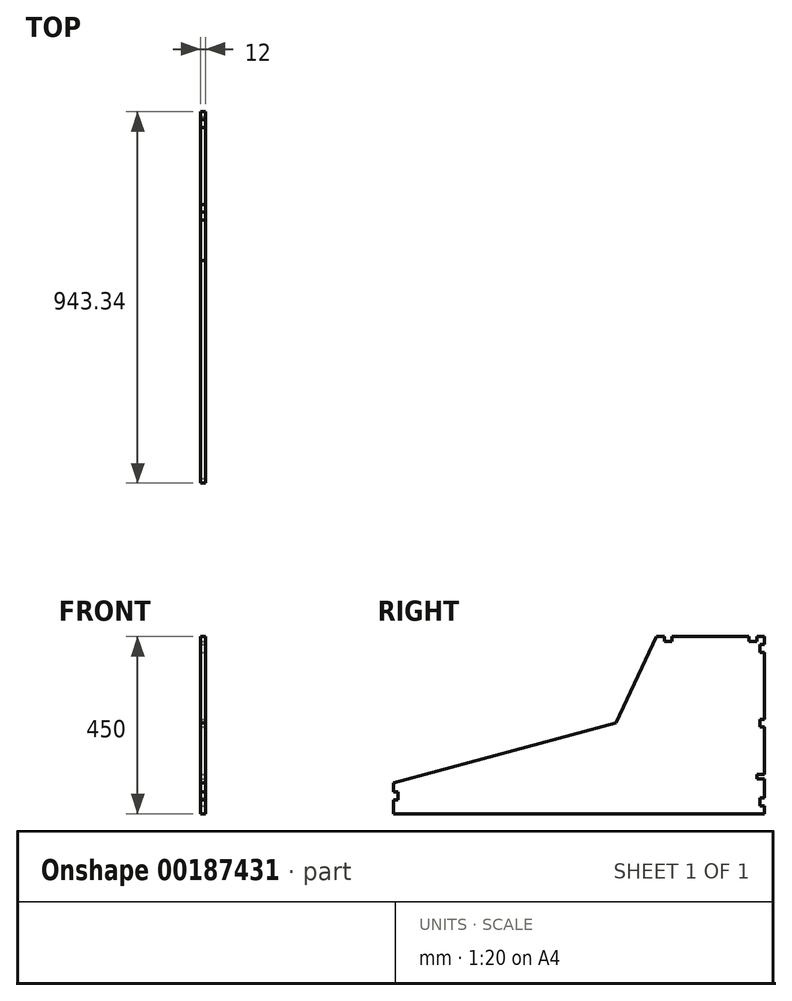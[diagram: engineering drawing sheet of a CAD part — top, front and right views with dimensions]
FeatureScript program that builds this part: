
annotation { "Feature Type Name" : "Feature", "Feature Type Description" : "" }
export const myFeature = defineFeature(function(context is Context, id is Id, definition is map)
    precondition{}
    {
        {
            var Q0;
            Q0=qCreatedBy(makeId("Right.planeOp"),FACE);
            var sketch = newSketch(context, id + "F0", { "sketchPlane" : qUnion([Q0])});
            skLineSegment(sketch, "E0.bottom", {"start": v(0, 0) * mm, "end": v(-738, 0) * mm});
            skLineSegment(sketch, "E0.top", {"start": v(0, 460) * mm, "end": v(-70.38, 460) * mm});
            skLineSegment(sketch, "E0.left", {"start": v(0, 0) * mm, "end": v(0, 460) * mm});
            skLineSegment(sketch, "E0.right", {"start": v(-738, 0) * mm, "end": v(-738, 90) * mm});
            skLineSegment(sketch, "E1", {"start": v(-172.22, 241.6) * mm, "end": v(-738, 90) * mm});
            skLineSegment(sketch, "E2.bottom", {"start": v(0, 0) * mm, "end": v(200, 0) * mm});
            skLineSegment(sketch, "E2.top", {"start": v(0, 460) * mm, "end": v(200, 460) * mm});
            skLineSegment(sketch, "E2.right", {"start": v(200, 0) * mm, "end": v(200, 460) * mm});
            skLineSegment(sketch, "E3", {"start": v(-70.38, 460) * mm, "end": v(-172.22, 241.6) * mm});
            skPoint(sketch, "E4.start.orphan", {"position": v(-850, 0) * mm});
            skSolve(sketch);
        }
        {
            var Q0;
            {var subQ4=sQuery(id+"F0.wireOp",EDGE,"E0.left");Q0=makeQuery(id+"F0.imprint","IMPRINT",FACE,{"disambiguationData":[TD([[makeQuery(id+"F0.imprint","IMPRINT",EDGE,{"derivedFrom":subQ4}),1.0]])]});}
            var Q1;
            {var subQ5=sQuery(id+"F0.wireOp",EDGE,"E1");Q1=makeQuery(id+"F0.imprint","IMPRINT",FACE,{"disambiguationData":[TD([[makeQuery(id+"F0.imprint","IMPRINT",EDGE,{"derivedFrom":subQ5}),1.0]])]});}
            var Q2;
            {var subQ0=sQuery(id+"F0.wireOp",EDGE,"gMac2zyo-H2hs-1GUk-txYp-QcEbhLNx8KIs");Q2=makeQuery(id+"F0.imprint","IMPRINT",FACE,{"disambiguationData":[TD([[makeQuery(id+"F0.imprint","IMPRINT",EDGE,{"derivedFrom":subQ0}),1.0]])]});}
            var Q3;
            Q3=makeQuery(id+"F0.imprint","IMPRINT",FACE,{"disambiguationData":[TD([[makeQuery(id+"F0.imprint","IMPRINT",EDGE,{"derivedFrom":sQuery(id+"F0.wireOp",EDGE,"E2.bottom")}),1.0]])]});
            var Q4;
            {var subQ2=sQuery(id+"F0.wireOp",EDGE,"E0.bottom");Q4=makeQuery(id+"F0.imprint","IMPRINT",FACE,{"disambiguationData":[TD([[makeQuery(id+"F0.imprint","IMPRINT",EDGE,{"derivedFrom":subQ2}),-1.0]])]});}
            var Q5;
            {var subQ0=sQuery(id+"F0.wireOp",EDGE,"gPEywheX-FLUY-aZ3r-SrXT-0dIdcKwJWZQq");Q5=makeQuery(id+"F0.imprint","IMPRINT",FACE,{"disambiguationData":[TD([[makeQuery(id+"F0.imprint","IMPRINT",EDGE,{"derivedFrom":subQ0}),1.0]])]});}
            extrude(context, id + "F1", {"entities" : qUnion([Q0, Q1, Q2, Q3, Q4, Q5]), "depth" : 12 * mm, "offsetDistance" : 25 * mm});
        }
        {
            var Q0;
            Q0=makeQuery(id+"F1.opExtrude","CAP_FACE",FACE,{"disambiguationData":[OSD([sQuery(id+"F0.wireOp",EDGE,"E0.bottom"),sQuery(id+"F0.wireOp",EDGE,"E0.top"),sQuery(id+"F0.wireOp",EDGE,"E0.right"),sQuery(id+"F0.wireOp",EDGE,"gMac2zyo-H2hs-1GUk-txYp-QcEbhLNx8KIs"),sQuery(id+"F0.wireOp",EDGE,"E1"),sQuery(id+"F0.wireOp",EDGE,"3gRgcraK-6qZi-Tpd4-jrs4-NTl78sH4m5cq"),sQuery(id+"F0.wireOp",EDGE,"E2.bottom"),sQuery(id+"F0.wireOp",EDGE,"E2.top"),sQuery(id+"F0.wireOp",EDGE,"E2.right")])],"isStart":false});
            var sketch = newSketch(context, id + "F2", { "sketchPlane" : qUnion([Q0])});
            skLineSegment(sketch, "E5.bottom", {"start": v(200, 20) * mm, "end": v(188, 20) * mm});
            skLineSegment(sketch, "E5.top", {"start": v(200, 40) * mm, "end": v(188, 40) * mm});
            skLineSegment(sketch, "E5.left", {"start": v(200, 20) * mm, "end": v(200, 40) * mm});
            skLineSegment(sketch, "E5.right", {"start": v(188, 20) * mm, "end": v(188, 40) * mm});
            skLineSegment(sketch, "E6.bottom", {"start": v(200, 220) * mm, "end": v(188, 220) * mm});
            skLineSegment(sketch, "E6.top", {"start": v(200, 240) * mm, "end": v(188, 240) * mm});
            skLineSegment(sketch, "E6.left", {"start": v(200, 220) * mm, "end": v(200, 240) * mm});
            skLineSegment(sketch, "E6.right", {"start": v(188, 220) * mm, "end": v(188, 240) * mm});
            skLineSegment(sketch, "E7.bottom", {"start": v(200, 410) * mm, "end": v(188, 410) * mm});
            skLineSegment(sketch, "E7.top", {"start": v(200, 430) * mm, "end": v(188, 430) * mm});
            skLineSegment(sketch, "E7.left", {"start": v(200, 410) * mm, "end": v(200, 430) * mm});
            skLineSegment(sketch, "E7.right", {"start": v(188, 410) * mm, "end": v(188, 430) * mm});
            skLineSegment(sketch, "E8.bottom", {"start": v(180, 460) * mm, "end": v(160, 460) * mm});
            skLineSegment(sketch, "E8.top", {"start": v(180, 438) * mm, "end": v(160, 438) * mm});
            skLineSegment(sketch, "E8.left", {"start": v(180, 460) * mm, "end": v(180, 438) * mm});
            skLineSegment(sketch, "E8.right", {"start": v(160, 460) * mm, "end": v(160, 438) * mm});
            skLineSegment(sketch, "E9.bottom", {"start": v(-55.04, 460) * mm, "end": v(-35.04, 460) * mm});
            skLineSegment(sketch, "E9.top", {"start": v(-55.04, 438) * mm, "end": v(-35.04, 438) * mm});
            skLineSegment(sketch, "E9.left", {"start": v(-55.04, 460) * mm, "end": v(-55.04, 438) * mm});
            skLineSegment(sketch, "E9.right", {"start": v(-35.04, 460) * mm, "end": v(-35.04, 438) * mm});
            skLineSegment(sketch, "E10", {"start": v(-55.04, 450) * mm, "end": v(-75.04, 450) * mm});
            skSolve(sketch);
        }
        {
            var Q0;
            Q0 = qSketchRegion(id + "F2", true);
            extrude(context, id + "F3", {"entities" : qUnion([Q0]), "operationType" : NewBodyOperationType.REMOVE, "oppositeDirection" : true, "depth" : 25 * mm});
        }
        {
            var Q0;
            {var subQ1=sQuery(id+"F0.wireOp",EDGE,"E2.top");var subQ7=sQuery(id+"F0.wireOp",EDGE,"E0.top");Q0=makeQuery(id+"F3.boolean.opBoolean","SPLIT",FACE,{"disambiguationData":[TD([makeQuery(id+"F3.opExtrude","SWEPT_FACE",FACE,{"disambiguationData":[OSD([sQuery(id+"F2.wireOp",EDGE,"E9.left")])]})])],"derivedFrom":makeQuery(id+"F1.opExtrude","SWEPT_FACE",FACE,{"disambiguationData":[OSD([subQ7,subQ1])]})});}
            var Q1;
            {var subQ1=sQuery(id+"F0.wireOp",EDGE,"E2.top");var subQ7=sQuery(id+"F0.wireOp",EDGE,"E0.top");Q1=makeQuery(id+"F3.boolean.opBoolean","SPLIT",FACE,{"disambiguationData":[TD([makeQuery(id+"F3.opExtrude","SWEPT_FACE",FACE,{"disambiguationData":[OSD([sQuery(id+"F2.wireOp",EDGE,"E8.right")])]})])],"derivedFrom":makeQuery(id+"F1.opExtrude","SWEPT_FACE",FACE,{"disambiguationData":[OSD([subQ7,subQ1])]})});}
            var Q2;
            {var subQ0=sQuery(id+"F0.wireOp",EDGE,"E2.right");var subQ1=sQuery(id+"F0.wireOp",EDGE,"E2.top");var subQ7=sQuery(id+"F0.wireOp",EDGE,"E0.top");Q2=makeQuery(id+"F3.boolean.opBoolean","SPLIT",FACE,{"disambiguationData":[TD([makeQuery(id+"F1.opExtrude","SWEPT_FACE",FACE,{"disambiguationData":[OSD([subQ0])]})])],"derivedFrom":makeQuery(id+"F1.opExtrude","SWEPT_FACE",FACE,{"disambiguationData":[OSD([subQ7,subQ1])]})});}
            extrude(context, id + "F4", {"entities" : qUnion([Q0, Q1, Q2]), "operationType" : NewBodyOperationType.REMOVE, "oppositeDirection" : true, "depth" : 10 * mm, "offsetDistance" : 25 * mm});
        }
        {
            var Q0;
            Q0=makeQuery(id+"F4.boolean.opBoolean","COPY",FACE,{"derivedFrom":makeQuery(id+"F4.opExtrude","SWEPT_FACE",FACE,{"disambiguationData":[OSD([sQuery(id+"F0.wireOp",EDGE,"E0.top"),sQuery(id+"F0.wireOp",EDGE,"3gRgcraK-6qZi-Tpd4-jrs4-NTl78sH4m5cq")])]})});
            extrude(context, id + "F5", {"entities" : qUnion([Q0]), "operationType" : NewBodyOperationType.REMOVE, "oppositeDirection" : true, "depth" : 25 * mm, "offsetDistance" : 25 * mm});
        }
        {
            var Q0;
            Q0=makeQuery(id+"F1.opExtrude","SWEPT_FACE",FACE,{"disambiguationData":[OSD([sQuery(id+"F0.wireOp",EDGE,"E0.right")])]});
            var sketch = newSketch(context, id + "F6", { "sketchPlane" : qUnion([Q0])});
            skLineSegment(sketch, "E11.bottom", {"start": v(12, 55) * mm, "end": v(0, 55) * mm});
            skLineSegment(sketch, "E11.top", {"start": v(12, 35) * mm, "end": v(0, 35) * mm});
            skLineSegment(sketch, "E11.left", {"start": v(12, 55) * mm, "end": v(12, 35) * mm});
            skLineSegment(sketch, "E11.right", {"start": v(0, 55) * mm, "end": v(0, 35) * mm});
            skPoint(sketch, "E11.middle", {"position": v(6, 45) * mm});
            skPoint(sketch, "E11.middle.positionSnap0", {"position": v(6, 90) * mm});
            skPoint(sketch, "E11.middle.positionSnap1", {"position": v(0, 45) * mm});
            skPoint(sketch, "E11.centerSnap0", {"position": v(6, 90) * mm});
            skPoint(sketch, "E11.centerSnap1", {"position": v(0, 45) * mm});
            skSolve(sketch);
        }
        {
            var Q0;
            Q0 = qSketchRegion(id + "F6", true);
            extrude(context, id + "F7", {"entities" : qUnion([Q0]), "operationType" : NewBodyOperationType.REMOVE, "oppositeDirection" : true, "depth" : 12 * mm, "offsetDistance" : 25 * mm});
        }
        {
            var Q0;
            Q0=makeQuery(id+"F1.opExtrude","CAP_FACE",FACE,{"disambiguationData":[OSD([sQuery(id+"F0.wireOp",EDGE,"E0.bottom"),sQuery(id+"F0.wireOp",EDGE,"E0.top"),sQuery(id+"F0.wireOp",EDGE,"E0.right"),sQuery(id+"F0.wireOp",EDGE,"E1"),sQuery(id+"F0.wireOp",EDGE,"E2.bottom"),sQuery(id+"F0.wireOp",EDGE,"E2.top"),sQuery(id+"F0.wireOp",EDGE,"E2.right"),sQuery(id+"F0.wireOp",EDGE,"E3")])],"isStart":false});
            var sketch = newSketch(context, id + "F8", { "sketchPlane" : qUnion([Q0])});
            skLineSegment(sketch, "E12.bottom", {"start": v(200, 100) * mm, "end": v(180, 100) * mm});
            skLineSegment(sketch, "E12.top", {"start": v(200, 88) * mm, "end": v(180, 88) * mm});
            skLineSegment(sketch, "E12.left", {"start": v(200, 100) * mm, "end": v(200, 88) * mm});
            skLineSegment(sketch, "E12.right", {"start": v(180, 100) * mm, "end": v(180, 88) * mm});
            skLineSegment(sketch, "E13", {"start": v(-738, 90) * mm, "end": v(-738, 0) * mm});
            skLineSegment(sketch, "E14", {"start": v(-172.22, 241.6) * mm, "end": v(-172.22, 0) * mm});
            skLineSegment(sketch, "E15", {"start": v(200, 0) * mm, "end": v(-738, 0) * mm});
            skLineSegment(sketch, "E16", {"start": v(200, 0) * mm, "end": v(200, 450) * mm});
            skLineSegment(sketch, "E17", {"start": v(200, 450) * mm, "end": v(-75.04, 450) * mm});
            skLineSegment(sketch, "E18", {"start": v(-738, 0) * mm, "end": v(-38, 0) * mm});
            skSolve(sketch);
        }
        {
            var Q0;
            Q0 = qSketchRegion(id + "F8", true);
            extrude(context, id + "F9", {"entities" : qUnion([Q0]), "operationType" : NewBodyOperationType.REMOVE, "oppositeDirection" : true, "depth" : 25 * mm, "offsetDistance" : 25 * mm});
        }
        {
            var Q0;
            Q0=makeQuery(id+"F1.opExtrude","CAP_FACE",FACE,{"disambiguationData":[OSD([sQuery(id+"F0.wireOp",EDGE,"E0.bottom"),sQuery(id+"F0.wireOp",EDGE,"E0.top"),sQuery(id+"F0.wireOp",EDGE,"E0.right"),sQuery(id+"F0.wireOp",EDGE,"E1"),sQuery(id+"F0.wireOp",EDGE,"E2.bottom"),sQuery(id+"F0.wireOp",EDGE,"E2.top"),sQuery(id+"F0.wireOp",EDGE,"E2.right"),sQuery(id+"F0.wireOp",EDGE,"E3")])],"isStart":false});
            var sketch = newSketch(context, id + "F10", { "sketchPlane" : qUnion([Q0])});
            skLineSegment(sketch, "E19", {"start": v(-75.04, 450) * mm, "end": v(-177.57, 230.14) * mm});
            skLineSegment(sketch, "E20", {"start": v(-177.57, 230.14) * mm, "end": v(-738, 79.97) * mm});
            skSolve(sketch);
        }
        {
            var Q0;
            {var subQ3=sQuery(id+"F10.wireOp",EDGE,"E20");Q0=makeQuery(id+"F10.imprint","IMPRINT",FACE,{"disambiguationData":[TD([[makeQuery(id+"F10.imprint","IMPRINT",EDGE,{"derivedFrom":subQ3}),-1.0]])]});}
            extrude(context, id + "F11", {"entities" : qUnion([Q0]), "operationType" : NewBodyOperationType.REMOVE, "oppositeDirection" : true, "depth" : 25 * mm, "offsetDistance" : 25 * mm});
        }
        {
            var Q0;
            Q0=makeQuery(id+"F1.opExtrude","CAP_FACE",FACE,{"disambiguationData":[OSD([sQuery(id+"F0.wireOp",EDGE,"E0.bottom"),sQuery(id+"F0.wireOp",EDGE,"E0.top"),sQuery(id+"F0.wireOp",EDGE,"E0.right"),sQuery(id+"F0.wireOp",EDGE,"E1"),sQuery(id+"F0.wireOp",EDGE,"E2.bottom"),sQuery(id+"F0.wireOp",EDGE,"E2.top"),sQuery(id+"F0.wireOp",EDGE,"E2.right"),sQuery(id+"F0.wireOp",EDGE,"E3")])],"isStart":false});
            var sketch = newSketch(context, id + "F12", { "sketchPlane" : qUnion([Q0])});
            skLineSegment(sketch, "E21", {"start": v(-177.57, 230.14) * mm, "end": v(-743.34, 78.54) * mm});
            skLineSegment(sketch, "E22", {"start": v(-743.34, 78.54) * mm, "end": v(-743.34, 0) * mm});
            skLineSegment(sketch, "E23", {"start": v(-743.34, 0) * mm, "end": v(-738, 0) * mm});
            skLineSegment(sketch, "E24", {"start": v(-743.34, 35) * mm, "end": v(-734.4, 35) * mm});
            skLineSegment(sketch, "E25", {"start": v(-743.34, 55) * mm, "end": v(-731.34, 55) * mm});
            skLineSegment(sketch, "E26", {"start": v(-731.34, 55) * mm, "end": v(-731.34, 35) * mm});
            skLineSegment(sketch, "E27", {"start": v(-731.34, 35) * mm, "end": v(-734.4, 35) * mm});
            skSolve(sketch);
        }
        {
            var Q0;
            {var subQ0=sQuery(id+"F12.wireOp",EDGE,"E21");var subQ4=sQuery(id+"F12.wireOp",EDGE,"E22");var subQ5=makeQuery(id+"F12.imprint","INTERSECT",VERTEX,{"derivedFrom":[subQ0,subQ4]});Q0=makeQuery(id+"F12.imprint","IMPRINT",FACE,{"disambiguationData":[TD([[makeQuery(id+"F12.imprint","IMPRINT",EDGE,{"disambiguationData":[TD([[subQ5,-1.0]])],"derivedFrom":subQ4}),1.0]])]});}
            var Q1;
            {var subQ0=sQuery(id+"F12.wireOp",EDGE,"E26");Q1=makeQuery(id+"F12.imprint","IMPRINT",FACE,{"disambiguationData":[TD([[makeQuery(id+"F12.imprint","IMPRINT",EDGE,{"derivedFrom":subQ0}),1.0]])]});}
            var Q2;
            {var subQ0=sQuery(id+"F12.wireOp",EDGE,"E23");Q2=makeQuery(id+"F12.imprint","IMPRINT",FACE,{"disambiguationData":[TD([[makeQuery(id+"F12.imprint","IMPRINT",EDGE,{"derivedFrom":subQ0}),1.0]])]});}
            extrude(context, id + "F13", {"entities" : qUnion([Q0, Q1, Q2]), "operationType" : NewBodyOperationType.ADD, "oppositeDirection" : true, "depth" : 12 * mm, "offsetDistance" : 25 * mm});
        }
    });
